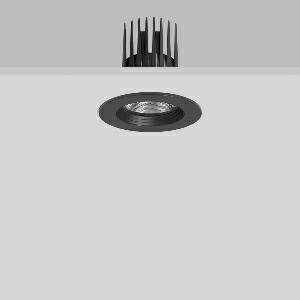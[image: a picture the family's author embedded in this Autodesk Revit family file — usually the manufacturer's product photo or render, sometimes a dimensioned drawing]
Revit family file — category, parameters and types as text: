
# Revit family: heledon_mini_e_901748_003_7ec6
name_source: partatom
category: Lighting Fixtures
units: mm (PartAtom-declared; Revit-internal decimal feet)

## family parameters
Cut with Voids When Loaded = No
Host = Face
Light Source = No
Part Type = Normal
Room Calculation Point = No
Round Connector Dimension = Use Diameter
Shared = No

## types (1)
- HELEDON mini E (1 x LED Modul 930, 3550 lm, 3000)
    Apparent Load = 29 VA
    Approval mark = CE
    CIE Flux Codes = 100 100 100 100 100
    Color Rendering = 90
    Color Temperature = 3000
    Default Elevation = 1800 mm
    Description = Series: HELEDON mini
Round recessed downlight. Housing: die-cast aluminium, powder-coated. Black plastic ring and recessed LED to prevent glare from the side. Optical assembly with reflector made of MIRO-Silver with 98% total light reflection for outstanding efficiency - can be changed without tools. Best colour rendering index Ra>90. Suitable for Recessed ceiling mounting. Installation without tools thanks to spring fastening system. Including separate LED converter with connecting cable 600 mm.High quality converter without flickering and stroboscopic effect. Through-wiring box (5 pole) available as accessory. The following accessories can be mounted without use of tools: interchangeable lenses, decorative glasses, honeycomb louvre, clear and frosted diffusers, white interchangeable plastic ring. 
Colour: deep black, matt (RAL 9005)
Diameter: 124 mm
Height: 3 mm
Cut-out diameter: 114 mm
Recess height: 170 mm
Luminaire: recess height: 120 mm
Lamp: LED
Socket: without socket
Colour temperature: 3000K
Colour rendering index (CRI): 92
System power: 29 W
Rated luminous flux: 3550 lm
Luminous efficiency: 122 lm/W
Control gear: Regulated power supply
Protection class: II
Type of protection: IP 20
    Height = 0 mm  [stored 0 ft]
    Lamp = 1 x LED Modul 930
    Lamp Light Flux = 3550 lm
    Lamp count = 1
    Length = 124 mm  [stored 0.406824 ft]
    Lifetime = 50000 h
    Luminous efficacy = 122 lm/W
    Manufacturer = RZB
    ModVariant = No
    Model = 901748.003
    Mounting Place = Ceiling
    Mounting Type = Recessed
    Number of Poles = 1
    OnlyDefault = Yes
    Power Factor = 1
    Product Name = HELEDON mini E
    Product group = Recessed downlights
    ProductGroupID = 402
    Protection Class = Protection class II
    Protection Degree = IP 20
    RLX_Detail_Level = 1
    RLX_Emergency_Light_Flux = 0 lm
    RLX_Emergency_Type = 0
    RLX_Emergency_Type_DB = No
    RlxData = <blob elided: 127521 chars, md5=933071f9>
    Socket = socket
    Standby Power = 0 W
    System Light Flux = 3550 lm
    System Power = 29 W
    Type Comments = Product without accessories
    Type Image = 901657.003.jpg
    URL = http://relux.com
    VarID = ---
    Voltage = 230 V
    Voltage Range = 220-240 V
    Weight = 0.00 kg
    Width = 0 mm  [stored 0 ft]

note: [stored X ft] marks values corroborated as IEEE doubles in the binary element streams (Revit-internal decimal feet)

## geometry (parser evidence)
native form markers: Blend x4, Sweep x12
no freeform markers — native parametric forms only
